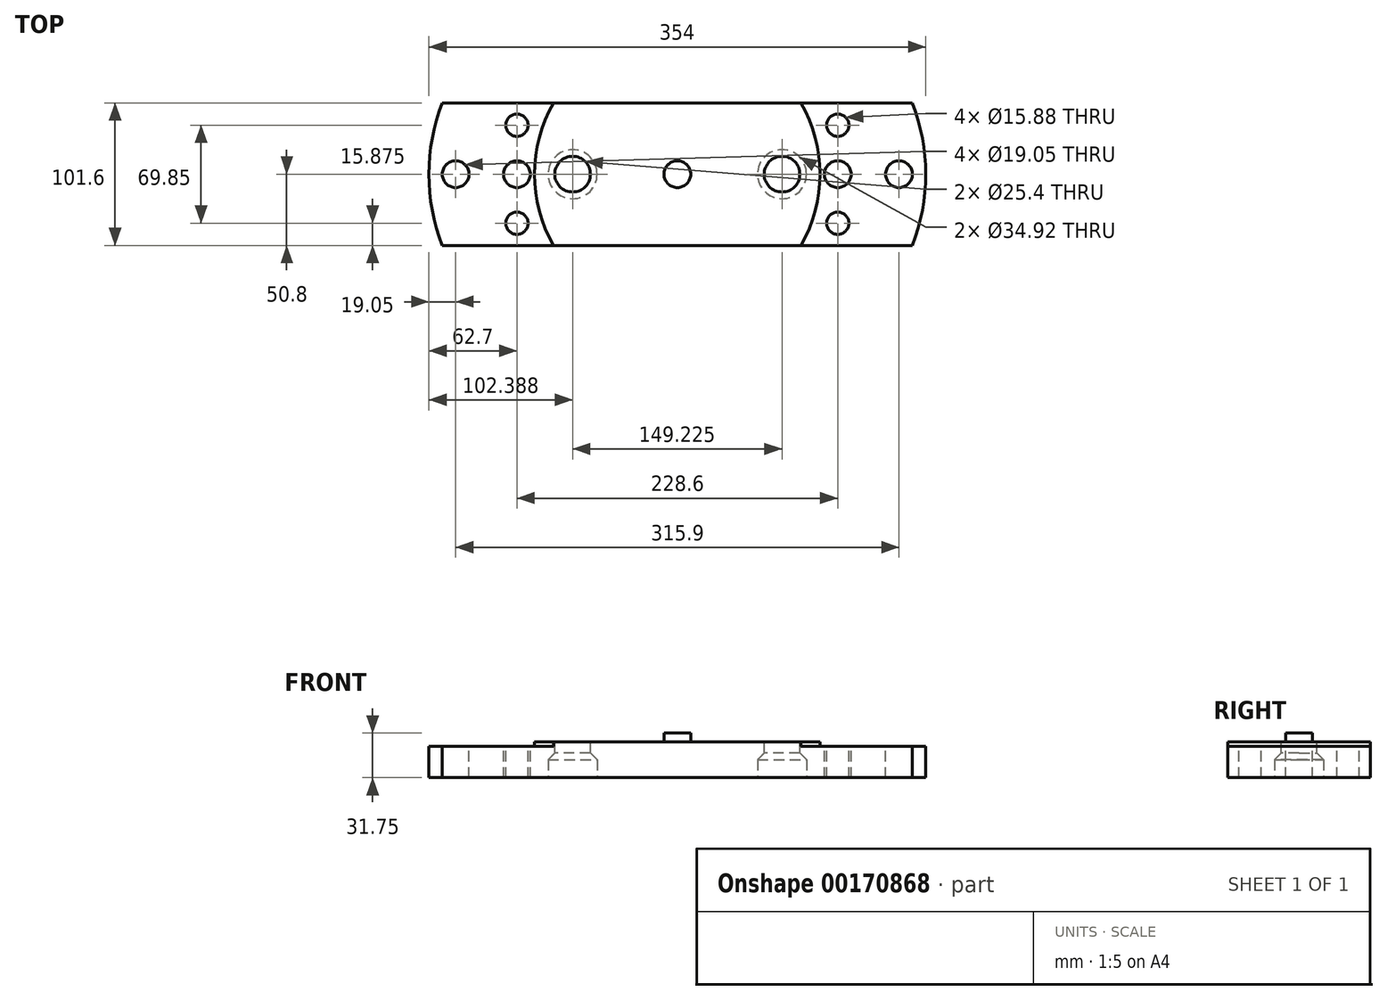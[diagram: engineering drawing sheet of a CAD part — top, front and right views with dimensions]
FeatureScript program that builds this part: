
annotation { "Feature Type Name" : "Feature", "Feature Type Description" : "" }
export const myFeature = defineFeature(function(context is Context, id is Id, definition is map)
    precondition{}
    {
        {
            var Q0;
            Q0=qCreatedBy(makeId("Top.planeOp"),FACE);
            var sketch = newSketch(context, id + "F0", { "sketchPlane" : qUnion([Q0])});
            skLineSegment(sketch, "E0.bottom", {"start": v(-167.47, 50.8) * mm, "end": v(167.47, 50.8) * mm});
            skLineSegment(sketch, "E0.top", {"start": v(-167.47, -50.8) * mm, "end": v(167.47, -50.8) * mm});
            skLineSegment(sketch, "E1", {"start": v(-177, 50.8) * mm, "end": v(177, -50.8) * mm, "construction": true});
            skArc(sketch, "E2", {"start": v(-167.47, 50.8) * mm, "mid": v(-177, 0) * mm, "end": v(-167.47, -50.8) * mm});
            skArc(sketch, "E3", {"start": v(167.47, -50.8) * mm, "mid": v(177, 0) * mm, "end": v(167.47, 50.8) * mm});
            skPoint(sketch, "E4.orphan", {"position": v(177, 50.8) * mm});
            skPoint(sketch, "E5.orphan", {"position": v(-177, -50.8) * mm});
            skSolve(sketch);
        }
        {
            var Q0;
            Q0 = qSketchRegion(id + "F0", true);
            extrude(context, id + "F1", {"entities" : qUnion([Q0]), "depth" : 31.75 * mm});
        }
        {
            var Q0;
            Q0=makeQuery(id+"F1.opExtrude","CAP_FACE",FACE,{"disambiguationData":[OSD([sQuery(id+"F0.wireOp",EDGE,"E0.bottom"),sQuery(id+"F0.wireOp",EDGE,"E0.top"),sQuery(id+"F0.wireOp",EDGE,"E2"),sQuery(id+"F0.wireOp",EDGE,"E3")])],"isStart":false});
            var sketch = newSketch(context, id + "F2", { "sketchPlane" : qUnion([Q0])});
            skCircle(sketch, "E6", {"center": v(0, 0) * mm, "radius": 9.53 * mm});
            skLineSegment(sketch, "E7.bottom", {"start": v(-186.14, 59.77) * mm, "end": v(191.28, 59.77) * mm});
            skLineSegment(sketch, "E7.top", {"start": v(-186.14, -69.43) * mm, "end": v(191.28, -69.43) * mm});
            skLineSegment(sketch, "E7.left", {"start": v(-186.14, 59.77) * mm, "end": v(-186.14, -69.43) * mm});
            skLineSegment(sketch, "E7.right", {"start": v(191.28, 59.77) * mm, "end": v(191.28, -69.43) * mm});
            skSolve(sketch);
        }
        {
            var Q0;
            Q0 = qSketchRegion(id + "F2", true);
            extrude(context, id + "F3", {"entities" : qUnion([Q0]), "operationType" : NewBodyOperationType.REMOVE, "oppositeDirection" : true, "depth" : 6.35 * mm});
        }
        {
            var Q0;
            Q0=makeQuery(id+"F3.boolean.opBoolean","COPY",FACE,{"derivedFrom":makeQuery(id+"F3.opExtrude","CAP_FACE",FACE,{"disambiguationData":[OSD([sQuery(id+"F2.wireOp",EDGE,"E6"),sQuery(id+"F2.wireOp",EDGE,"E7.bottom"),sQuery(id+"F2.wireOp",EDGE,"E7.top"),sQuery(id+"F2.wireOp",EDGE,"E7.left"),sQuery(id+"F2.wireOp",EDGE,"E7.right")])],"isStart":false})});
            var sketch = newSketch(context, id + "F4", { "sketchPlane" : qUnion([Q0])});
            skArc(sketch, "E8", {"start": v(-88.13, 50.8) * mm, "mid": v(-101.74, 0) * mm, "end": v(-88.13, -50.8) * mm});
            skArc(sketch, "E9", {"start": v(88.07, -50.8) * mm, "mid": v(101.67, 0) * mm, "end": v(88.07, 50.8) * mm});
            skCircle(sketch, "E10", {"center": v(0, 0) * mm, "radius": 9.53 * mm});
            skLineSegment(sketch, "E11.bottom", {"start": v(-188.99, 78.6) * mm, "end": v(193.62, 78.6) * mm});
            skLineSegment(sketch, "E11.top", {"start": v(-188.99, -80.36) * mm, "end": v(193.62, -80.36) * mm});
            skLineSegment(sketch, "E11.left", {"start": v(-188.99, 78.6) * mm, "end": v(-188.99, -80.36) * mm});
            skLineSegment(sketch, "E11.right", {"start": v(193.62, 78.6) * mm, "end": v(193.62, -80.36) * mm});
            skSolve(sketch);
        }
        {
            var Q0;
            {var subQ0=sQuery(id+"F4.wireOp",EDGE,"E8");Q0=makeQuery(id+"F4.imprint","IMPRINT",FACE,{"disambiguationData":[TD([[makeQuery(id+"F4.imprint","IMPRINT",EDGE,{"derivedFrom":subQ0}),-1.0]])]});}
            var Q1;
            {var subQ0=sQuery(id+"F4.wireOp",EDGE,"E9");Q1=makeQuery(id+"F4.imprint","IMPRINT",FACE,{"disambiguationData":[TD([[makeQuery(id+"F4.imprint","IMPRINT",EDGE,{"derivedFrom":subQ0}),-1.0]])]});}
            var Q2;
            Q2=makeQuery(id+"F4.imprint","IMPRINT",FACE,{"disambiguationData":[TD([[makeQuery(id+"F4.imprint","IMPRINT",EDGE,{"derivedFrom":sQuery(id+"F4.wireOp",EDGE,"E11.bottom")}),-1.0]])]});
            extrude(context, id + "F5", {"entities" : qUnion([Q0, Q1, Q2]), "operationType" : NewBodyOperationType.REMOVE, "oppositeDirection" : true, "depth" : 3.17 * mm});
        }
        {
            var Q0;
            Q0=makeQuery(id+"F3.boolean.opBoolean","COPY",FACE,{"derivedFrom":makeQuery(id+"F3.opExtrude","CAP_FACE",FACE,{"disambiguationData":[OSD([sQuery(id+"F2.wireOp",EDGE,"E6"),sQuery(id+"F2.wireOp",EDGE,"E7.bottom"),sQuery(id+"F2.wireOp",EDGE,"E7.top"),sQuery(id+"F2.wireOp",EDGE,"E7.left"),sQuery(id+"F2.wireOp",EDGE,"E7.right")])],"isStart":false})});
            var sketch = newSketch(context, id + "F6", { "sketchPlane" : qUnion([Q0])});
            skCircle(sketch, "E12", {"center": v(-74.61, 0) * mm, "radius": 12.7 * mm});
            skCircle(sketch, "E13", {"center": v(74.61, 0) * mm, "radius": 12.7 * mm});
            skCircle(sketch, "E14", {"center": v(114.3, 0) * mm, "radius": 9.53 * mm});
            skCircle(sketch, "E15", {"center": v(157.95, 0) * mm, "radius": 9.53 * mm});
            skCircle(sketch, "E16", {"center": v(-114.3, 0) * mm, "radius": 9.53 * mm});
            skCircle(sketch, "E17", {"center": v(-157.95, 0) * mm, "radius": 9.53 * mm});
            skCircle(sketch, "E18", {"center": v(-114.3, 34.93) * mm, "radius": 7.94 * mm});
            skCircle(sketch, "E19", {"center": v(-114.3, -34.93) * mm, "radius": 7.94 * mm});
            skCircle(sketch, "E20", {"center": v(114.3, 34.93) * mm, "radius": 7.94 * mm});
            skCircle(sketch, "E21", {"center": v(114.3, -34.93) * mm, "radius": 7.94 * mm});
            skSolve(sketch);
        }
        {
            var Q0;
            Q0 = qSketchRegion(id + "F6", true);
            extrude(context, id + "F7", {"entities" : qUnion([Q0]), "operationType" : NewBodyOperationType.REMOVE, "oppositeDirection" : true, "depth" : 25.4 * mm});
        }
        {
            var Q0;
            Q0=makeQuery(id+"F1.opExtrude","CAP_FACE",FACE,{"disambiguationData":[OSD([sQuery(id+"F0.wireOp",EDGE,"E0.bottom"),sQuery(id+"F0.wireOp",EDGE,"E0.top"),sQuery(id+"F0.wireOp",EDGE,"E2"),sQuery(id+"F0.wireOp",EDGE,"E3")])],"isStart":true});
            var sketch = newSketch(context, id + "F8", { "sketchPlane" : qUnion([Q0])});
            skCircle(sketch, "E22", {"center": v(-74.61, 0) * mm, "radius": 17.46 * mm});
            skCircle(sketch, "E23", {"center": v(74.61, 0) * mm, "radius": 17.46 * mm});
            skSolve(sketch);
        }
        {
            var Q0;
            Q0 = qSketchRegion(id + "F8", true);
            extrude(context, id + "F9", {"entities" : qUnion([Q0]), "operationType" : NewBodyOperationType.REMOVE, "oppositeDirection" : true, "depth" : 12.7 * mm});
        }
        {
            var Q0;
            Q0=makeQuery(id+"F9.boolean.opBoolean","INTERSECT",EDGE,{"derivedFrom":[makeQuery(id+"F7.boolean.opBoolean","COPY",FACE,{"derivedFrom":makeQuery(id+"F7.opExtrude","SWEPT_FACE",FACE,{"disambiguationData":[OSD([sQuery(id+"F6.wireOp",EDGE,"E13")])]})}),makeQuery(id+"F9.opExtrude","CAP_FACE",FACE,{"disambiguationData":[OSD([sQuery(id+"F8.wireOp",EDGE,"E23")])],"isStart":false})]});
            chamfer(context, id + "F10", {"entities" : qUnion([Q0]), "width" : 4.78 * mm, "tangentPropagation" : true});
        }
        {
            var Q0;
            Q0=makeQuery(id+"F9.boolean.opBoolean","INTERSECT",EDGE,{"derivedFrom":[makeQuery(id+"F7.boolean.opBoolean","COPY",FACE,{"derivedFrom":makeQuery(id+"F7.opExtrude","SWEPT_FACE",FACE,{"disambiguationData":[OSD([sQuery(id+"F6.wireOp",EDGE,"E12")])]})}),makeQuery(id+"F9.opExtrude","CAP_FACE",FACE,{"disambiguationData":[OSD([sQuery(id+"F8.wireOp",EDGE,"E22")])],"isStart":false})]});
            chamfer(context, id + "F11", {"entities" : qUnion([Q0]), "width" : 4.76 * mm, "tangentPropagation" : true});
        }
    });
